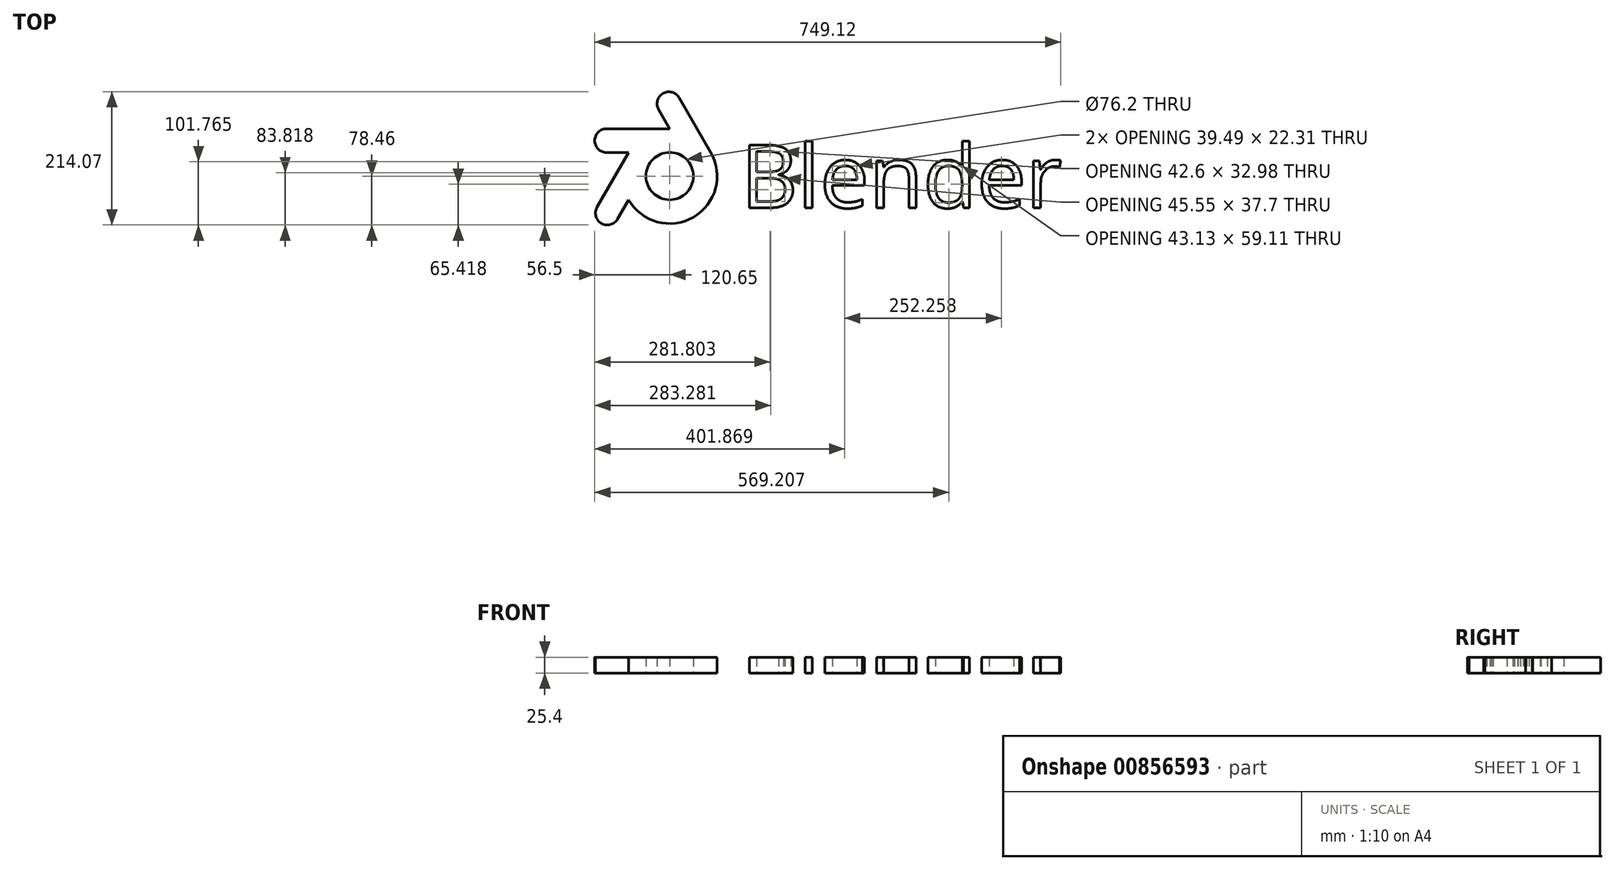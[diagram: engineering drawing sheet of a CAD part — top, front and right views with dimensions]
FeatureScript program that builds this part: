
annotation { "Feature Type Name" : "Feature", "Feature Type Description" : "" }
export const myFeature = defineFeature(function(context is Context, id is Id, definition is map)
    precondition{}
    {
        {
            var Q0;
            Q0=qCreatedBy(makeId("Top.planeOp"),FACE);
            var sketch = newSketch(context, id + "F0", { "sketchPlane" : qUnion([Q0])});
            skCircle(sketch, "E0", {"center": v(0, 0) * mm, "radius": 76.2 * mm});
            skCircle(sketch, "E1", {"center": v(0, 0) * mm, "radius": 38.1 * mm});
            skLineSegment(sketch, "E2", {"start": v(0, 76.2) * mm, "end": v(-101.6, 76.2) * mm});
            skLineSegment(sketch, "E3", {"start": v(0, 38.1) * mm, "end": v(-101.6, 38.1) * mm});
            skLineSegment(sketch, "E4", {"start": v(-66, 38.1) * mm, "end": v(-116.8, -49.89) * mm});
            skLineSegment(sketch, "E5", {"start": v(-33, 19.05) * mm, "end": v(-83.8, -68.94) * mm});
            skLineSegment(sketch, "E6", {"start": v(66, 38.1) * mm, "end": v(15.2, 126.09) * mm});
            skLineSegment(sketch, "E7", {"start": v(33, 19.05) * mm, "end": v(-17.8, 107.04) * mm});
            skArc(sketch, "E8", {"start": v(-17.8, 107.04) * mm, "mid": v(-10.83, 133.06) * mm, "end": v(15.2, 126.09) * mm});
            skArc(sketch, "E9", {"start": v(-101.6, 38.1) * mm, "mid": v(-120.65, 57.15) * mm, "end": v(-101.6, 76.2) * mm});
            skArc(sketch, "E10", {"start": v(-83.8, -68.94) * mm, "mid": v(-109.82, -75.91) * mm, "end": v(-116.8, -49.89) * mm});
            skSolve(sketch);
        }
        {
            var Q0;
            {var subQ3=sQuery(id+"F0.wireOp",EDGE,"E6");Q0=makeQuery(id+"F0.imprint","IMPRINT",FACE,{"disambiguationData":[TD([[makeQuery(id+"F0.imprint","IMPRINT",EDGE,{"derivedFrom":subQ3}),1.0]])]});}
            var Q1;
            {var subQ3=sQuery(id+"F0.wireOp",EDGE,"E0");var subQ7=makeQuery(id+"F0.imprint","INTERSECT",VERTEX,{"derivedFrom":[subQ3,sQuery(id+"F0.wireOp",EDGE,"E6")]});Q1=makeQuery(id+"F0.imprint","IMPRINT",FACE,{"disambiguationData":[TD([[makeQuery(id+"F0.imprint","IMPRINT",EDGE,{"disambiguationData":[TD([[subQ7,1.0]])],"derivedFrom":subQ3}),1.0]])]});}
            var Q2;
            {var subQ0=sQuery(id+"F0.wireOp",EDGE,"E3");var subQ5=sQuery(id+"F0.wireOp",EDGE,"E1");var subQ6=makeQuery(id+"F0.imprint","INTERSECT",VERTEX,{"derivedFrom":[subQ5,subQ0]});Q2=makeQuery(id+"F0.imprint","IMPRINT",FACE,{"disambiguationData":[TD([[makeQuery(id+"F0.imprint","IMPRINT",EDGE,{"disambiguationData":[TD([[subQ6,-1.0]])],"derivedFrom":subQ5}),-1.0]])]});}
            var Q3;
            {var subQ3=sQuery(id+"F0.wireOp",EDGE,"E3");var subQ5=sQuery(id+"F0.wireOp",EDGE,"E1");var subQ6=makeQuery(id+"F0.imprint","INTERSECT",VERTEX,{"derivedFrom":[subQ5,subQ3]});Q3=makeQuery(id+"F0.imprint","IMPRINT",FACE,{"disambiguationData":[TD([[makeQuery(id+"F0.imprint","IMPRINT",EDGE,{"disambiguationData":[TD([[subQ6,1.0]])],"derivedFrom":subQ5}),-1.0]])]});}
            var Q4;
            {var subQ0=sQuery(id+"F0.wireOp",EDGE,"E4");Q4=makeQuery(id+"F0.imprint","IMPRINT",FACE,{"disambiguationData":[TD([[makeQuery(id+"F0.imprint","IMPRINT",EDGE,{"derivedFrom":subQ0}),1.0]])]});}
            var Q5;
            {var subQ0=sQuery(id+"F0.wireOp",EDGE,"E2");Q5=makeQuery(id+"F0.imprint","IMPRINT",FACE,{"disambiguationData":[TD([[makeQuery(id+"F0.imprint","IMPRINT",EDGE,{"derivedFrom":subQ0}),1.0]])]});}
            extrude(context, id + "F1", {"entities" : qUnion([Q0, Q1, Q2, Q3, Q4, Q5]), "depth" : 25.4 * mm, "offsetDistance" : 25.4 * mm});
        }
        {
            var Q0;
            Q0=qCreatedBy(makeId("Top.planeOp"),FACE);
            var sketch = newSketch(context, id + "F2", { "sketchPlane" : qUnion([Q0])});
            skText(sketch, "E11", { "text": "Blender", "fontName": "OpenSans-Regular.ttf"});
            const initialGuessF2  = {"E11": [0.1143, -0.0508, 1, 0, 0.1016]};
            skSetInitialGuess(sketch, initialGuessF2);
            skSolve(sketch);
        }
        {
            var Q0;
            Q0=makeQuery(id+"F2.imprint","IMPRINT",FACE,{"disambiguationData":[TD([[makeQuery(id+"F2.imprint","IMPRINT",EDGE,{"derivedFrom":sQuery(id+"F2.wireOp",EDGE,"E11.sketch_text.stroke-0")}),-1.0]])]});
            var Q1;
            Q1=makeQuery(id+"F2.imprint","IMPRINT",FACE,{"disambiguationData":[TD([[makeQuery(id+"F2.imprint","IMPRINT",EDGE,{"derivedFrom":sQuery(id+"F2.wireOp",EDGE,"E11.sketch_text.stroke-25")}),-1.0]])]});
            var Q2;
            Q2=makeQuery(id+"F2.imprint","IMPRINT",FACE,{"disambiguationData":[TD([[makeQuery(id+"F2.imprint","IMPRINT",EDGE,{"derivedFrom":sQuery(id+"F2.wireOp",EDGE,"E11.sketch_text.stroke-29")}),-1.0]])]});
            var Q3;
            Q3=makeQuery(id+"F2.imprint","IMPRINT",FACE,{"disambiguationData":[TD([[makeQuery(id+"F2.imprint","IMPRINT",EDGE,{"derivedFrom":sQuery(id+"F2.wireOp",EDGE,"E11.sketch_text.stroke-48")}),-1.0]])]});
            var Q4;
            Q4=makeQuery(id+"F2.imprint","IMPRINT",FACE,{"disambiguationData":[TD([[makeQuery(id+"F2.imprint","IMPRINT",EDGE,{"derivedFrom":sQuery(id+"F2.wireOp",EDGE,"E11.sketch_text.stroke-65")}),-1.0]])]});
            var Q5;
            Q5=makeQuery(id+"F2.imprint","IMPRINT",FACE,{"disambiguationData":[TD([[makeQuery(id+"F2.imprint","IMPRINT",EDGE,{"derivedFrom":sQuery(id+"F2.wireOp",EDGE,"E11.sketch_text.stroke-89")}),-1.0]])]});
            var Q6;
            Q6=makeQuery(id+"F2.imprint","IMPRINT",FACE,{"disambiguationData":[TD([[makeQuery(id+"F2.imprint","IMPRINT",EDGE,{"derivedFrom":sQuery(id+"F2.wireOp",EDGE,"E11.sketch_text.stroke-108")}),-1.0]])]});
            extrude(context, id + "F3", {"entities" : qUnion([Q0, Q1, Q2, Q3, Q4, Q5, Q6]), "depth" : 25.4 * mm, "offsetDistance" : 25.4 * mm});
        }
    });
